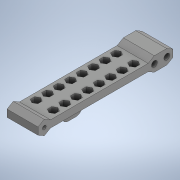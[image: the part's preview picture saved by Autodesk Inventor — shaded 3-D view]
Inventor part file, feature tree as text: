
AUTODESK INVENTOR PART (.ipt)
format: ipt  version: 2020 (Build 240168000, 168)  size: 489,472 bytes
history: native  units: in
note: dims shown in document units (in); Inventor stores cm internally (conversion verified against a paired STEP export)
features: sketch x7, extrude x6, projected_geometry x4, plane x2, mirror x1, fillet x1
ambient origin geometry x8: Origin, YZ Plane, XZ Plane, XY Plane, X Axis, Y Axis, Z Axis, Center Point
bodies: Solid1 (feature_tree)
feature tree (21):
  extrude  "Extrusion1"  Depth=3.4256in
  plane  "Work Plane1"
  extrude  "Extrusion2"  Depth=0.7874in
  sketch  "Sketch4"  dims[d4=0.0in d5=0.0827in]
  extrude  "Extrusion4"  Depth=0.0827in
  plane  "Work Plane2"
  extrude  "Extrusion6"  Depth=3.1106in
  mirror  "Mirror2"
  extrude  "Extrusion7"  Depth=0.315in
  extrude  "Extrusion8"  Depth=0.2362in
  fillet  "Fillet1"  [1 undecoded]
  sketch  "Sketch1"  dims[d0=0.1818in d1=3.4256in]
  sketch  "Sketch2"  dims[d2=0.0945in d3=0.7874in]
  sketch  "Sketch5"  dims[d6=0.7874in d7=0.0in d28=3.1106in]
  sketch  "Sketch7"  dims[d29=0.315in d31=0.315in]
  projected_geometry  "Projected Loop7"
  projected_geometry  "Projected Loop8"
  sketch  "Sketch8"  dims[d33=0.1476in d34=0.2362in d35=0.0in]
  projected_geometry  "Projected Loop9"
  sketch  "Sketch10"  dims[d38=0.315in d39=0.2756in d40=-0.3092in d41=0.0787in d42=0.0787in d43=0.0787in d44=3.1496in d46=0.2913in d47=0.3937in d49=0.3937in d51=3.1496in d53=0.2913in d54=0.3937in d56=0.3937in d58=0.0in d59=0.0in d60=1.0994in d61=0.1378in d63=1.1811in d64=0.1575in d65=0.0in d66=0.126in d67=0.1575in]
  projected_geometry  "Projected Loop10"
note: 1 required parameter value undecoded (feature->parameter linkage not recoverable at this tier; creation-order binding heuristic only, values carry confidence <= 0.55)
